# Revit family: Fixture_Support_EZCarry_Horizontal-Zurn-Z1201-N_4-FMBO
name_source: partatom
category: Plumbing Fixtures
units: mm (PartAtom-declared; Revit-internal decimal feet)

## family parameters
Always vertical = Yes
Cut with Voids When Loaded = No
Maintain Annotation Orientation = No
OmniClass Number = 23.45.55.11
OmniClass Title = Sanitary Components
Part Type = Normal
Room Calculation Point = No
Round Connector Dimension = Use Radius
Shared = No
Work Plane-Based = No

## types (4) — shared parameters
Assembly Code = D2030400
CW Connection = No
Coupling Material = ABS - Zurn - Plastic
Coupling Range = 2 "
Default Elevation = 20 "
HW Connection = No
Hardware = Steel - Zurn  - Galvanized
Height = 10.75 "
Left Connector = Yes
Main Material = Iron - Zurn - Cast - Painted - Blue
Manufacturer = Zurn Water, LLC
Manufacurer Brand = Zurn
Model = Z1201-N_4-FMBO
Modified Date = 02/6/2026
Product Documentation Link = https://files.zurn.com
Product Page URL = https://www.zurn.com
Product data url = https://www.bimobject.com
URL = www.zurn.com
Vent Connection = Yes
Vent Radius = 1 "
WFU = 1
Waste Connection = Yes
Water Closet Nominal radius = 1.5 "
Water Closet outer radius = 1.75 "
zero-valued in all types: CWFU, HWFU

## per-type parameters (varying)
| type | Approx. Weight (Lbs) | Connector | Connector Radius | Description | Dimension_K | Dimension_N | Half side Length A | Half side Length_B | Horizontal Pipe length | Pipe Size_A Inside Diameter | Pipe Size_A Inside Radius | Pipe Size_A Nominal Diameter | Pipe Size_A Outer Diameter | Pipe Size_A Outer Radius | Type Comments |
| Z1201-NR4_FMBO | 38.00 lb | 2.313 " | 2 " | EZCARRY® ADJUSTABLE HORIZONTAL HIGH PERFORMANCE SIPHON JET NO-HUB WATER CLOSET CARRIER SYSTEM W/ FLOOR MOUNT BACK OUTLET FIXTURE SUPPORT | 4.126 " | 8.563 " | 9.125 " | 3.125 " | 12.25 " | 4.026 " | 2.013 " | 4 " | 4.5 " | 2.25 " | 4 Inch No-Hub Right Hand Inlet with Flow to Left |
| Z1201-NL4_FMBO | 38.00 lb | 2.375 " | 2 " | EZCARRY® ADJUSTABLE HORIZONTAL HIGH PERFORMANCE SIPHON JET NO-HUB WATER CLOSET CARRIER SYSTEM W/ FLOOR MOUNT BACK OUTLET FIXTURE SUPPORT | 4.125 " | 8.563 " | 9.125 " | 3.125 " | 12.25 " | 4.026 " | 2.013 " | 4 " | 4.5 " | 2.25 " | 4 Inch No-Hub Left Hand Inlet with Flow to Right |
| Z1201-NR3_FMBO | 35.00 lb | 2.375 " | 1.5 " | EZCARRY® ADJUSTABLE HORIZONTAL HIGH PERFORMANCE SIPHON JET NO-HUB WATER CLOSET CARRIER SYSTEM W/  FLOOR MOUNT BACK OUTLET FIXTURE SUPPORT | 4.125 " | 7.188 " | 9 " | 2.5 " | 11.5 " | 3.068 " | 1.534 " | 3 " | 3.5 " | 1.75 " | 3 Inch No-Hub Right Hand Inlet with Flow to Left |
| Z1201-NL3_FMBO | 35.00 lb | 2.375 " | 1.5 " | EZCARRY® ADJUSTABLE HORIZONTAL HIGH PERFORMANCE SIPHON JET NO-HUB WATER CLOSET CARRIER SYSTEM W/  FLOOR MOUNT BACK OUTLET FIXTURE SUPPORT | 4.125 " | 7.188 " | 9 " | 2.5 " | 11.5 " | 3.068 " | 1.534 " | 3 " | 3.5 " | 1.75 " | 3 Inch No-Hub Left Hand Inlet with Flow to Right" |

type visibility flags: 4 boolean params named "<type name>" — each type sets only its own to Yes (folded from table)

## geometry (parser evidence)
native form markers: Blend x8, Sweep x37
no freeform markers — native parametric forms only
